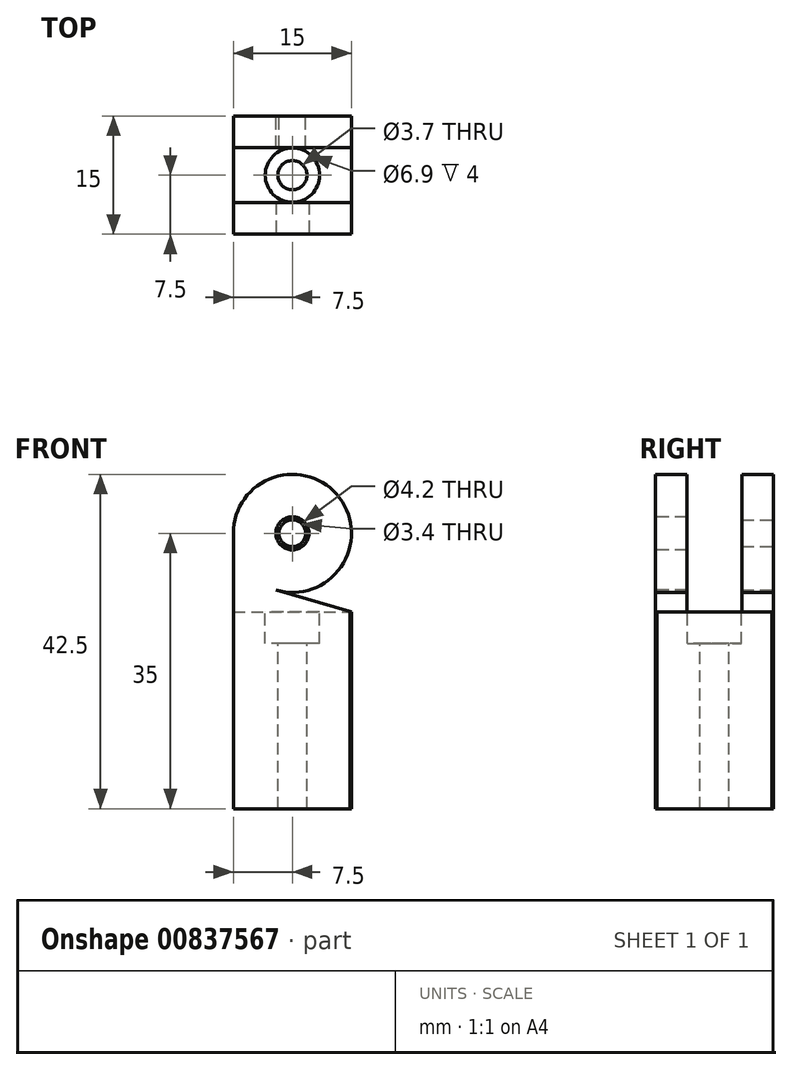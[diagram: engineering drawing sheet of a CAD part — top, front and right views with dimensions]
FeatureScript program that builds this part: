
annotation { "Feature Type Name" : "Feature", "Feature Type Description" : "" }
export const myFeature = defineFeature(function(context is Context, id is Id, definition is map)
    precondition{}
    {
        {
            var Q0;
            Q0=qCreatedBy(makeId("Top.planeOp"),FACE);
            var sketch = newSketch(context, id + "F0", { "sketchPlane" : qUnion([Q0])});
            skLineSegment(sketch, "E0", {"start": v(0, 0) * mm, "end": v(7.5, 0) * mm});
            skLineSegment(sketch, "E1", {"start": v(7.5, 0) * mm, "end": v(7.5, 7.5) * mm});
            skLineSegment(sketch, "E2", {"start": v(7.5, 7.5) * mm, "end": v(-7.5, 7.5) * mm});
            skLineSegment(sketch, "E3", {"start": v(-7.5, 7.5) * mm, "end": v(-7.5, -7.5) * mm});
            skLineSegment(sketch, "E4", {"start": v(-7.5, -7.5) * mm, "end": v(7.5, -7.5) * mm});
            skLineSegment(sketch, "E5", {"start": v(7.5, -7.5) * mm, "end": v(7.5, 0) * mm});
            skSolve(sketch);
        }
        {
            var Q0;
            Q0=makeQuery(id+"F0.imprint","IMPRINT",FACE,{"disambiguationData":[TD([[makeQuery(id+"F0.imprint","IMPRINT",EDGE,{"derivedFrom":sQuery(id+"F0.wireOp",EDGE,"E1")}),1.0]])]});
            extrude(context, id + "F1", {"entities" : qUnion([Q0]), "depth" : 25 * mm, "offsetDistance" : 25 * mm});
        }
        {
            var Q0;
            Q0=makeQuery(id+"F1.opExtrude","CAP_FACE",FACE,{"disambiguationData":[OSD([sQuery(id+"F0.wireOp",EDGE,"E1"),sQuery(id+"F0.wireOp",EDGE,"E2"),sQuery(id+"F0.wireOp",EDGE,"E3"),sQuery(id+"F0.wireOp",EDGE,"E4"),sQuery(id+"F0.wireOp",EDGE,"E5")])],"isStart":false});
            var sketch = newSketch(context, id + "F2", { "sketchPlane" : qUnion([Q0])});
            skPoint(sketch, "E6", {"position": v(0, 0) * mm});
            skSolve(sketch);
        }
        {
            var Q0;
            Q0=sQuery(id+"F2.wireOp",VERTEX,"E6");
            var Q1;
            Q1=makeQuery(id+"F1.opExtrude","SWEPT_BODY",BODY,{"disambiguationData":[OSD([sQuery(id+"F0.wireOp",EDGE,"E1"),sQuery(id+"F0.wireOp",EDGE,"E2"),sQuery(id+"F0.wireOp",EDGE,"E3"),sQuery(id+"F0.wireOp",EDGE,"E4"),sQuery(id+"F0.wireOp",EDGE,"E5")])]});
            hole(context, id + "F3", {"style" : HoleStyle.C_BORE, "endStyle" : HoleEndStyle.THROUGH, "holeDiameter" : 3.7 * mm, "cBoreDiameter" : 6.9 * mm, "cBoreDepth" : 4 * mm, "majorDiameter" : 5 * mm, "isTappedThrough" : true, "tappedDepth" : 12 * mm, "tapClearance" : 3, "locations" : qUnion([Q0]), "scope" : qUnion([Q1])});
        }
        {
            var Q0;
            Q0=makeQuery(id+"F1.opExtrude","SWEPT_FACE",FACE,{"disambiguationData":[OSD([sQuery(id+"F0.wireOp",EDGE,"E2")])]});
            var sketch = newSketch(context, id + "F4", { "sketchPlane" : qUnion([Q0])});
            skLineSegment(sketch, "E7", {"start": v(7.5, 25) * mm, "end": v(7.5, 35) * mm});
            skLineSegment(sketch, "E8", {"start": v(7.5, 35) * mm, "end": v(0, 35) * mm});
            skCircle(sketch, "E9", {"center": v(0, 35) * mm, "radius": 7.5 * mm});
            skLineSegment(sketch, "E10", {"start": v(-7.5, 25) * mm, "end": v(2.1, 27.8) * mm});
            skSolve(sketch);
        }
        {
            var Q0;
            {var subQ0=sQuery(id+"F4.wireOp",EDGE,"E7");Q0=makeQuery(id+"F4.imprint","IMPRINT",FACE,{"disambiguationData":[TD([[makeQuery(id+"F4.imprint","IMPRINT",EDGE,{"derivedFrom":subQ0}),1.0]])]});}
            var Q1;
            {var subQ0=sQuery(id+"F4.wireOp",EDGE,"E9");var subQ1=makeQuery(id+"F4.imprint","INTERSECT",VERTEX,{"derivedFrom":[sQuery(id+"F4.wireOp",EDGE,"E7"),subQ0]});Q1=makeQuery(id+"F4.imprint","IMPRINT",FACE,{"disambiguationData":[TD([[makeQuery(id+"F4.imprint","IMPRINT",EDGE,{"disambiguationData":[TD([[subQ1,-1.0]])],"derivedFrom":subQ0}),1.0]])]});}
            extrude(context, id + "F5", {"entities" : qUnion([Q0, Q1]), "operationType" : NewBodyOperationType.ADD, "oppositeDirection" : true, "depth" : 4 * mm, "offsetDistance" : 25 * mm});
        }
        {
            var Q0;
            Q0=makeQuery(id+"F1.opExtrude","SWEPT_FACE",FACE,{"disambiguationData":[OSD([sQuery(id+"F0.wireOp",EDGE,"E4")])]});
            var sketch = newSketch(context, id + "F6", { "sketchPlane" : qUnion([Q0])});
            skLineSegment(sketch, "E11", {"start": v(-7.5, 25) * mm, "end": v(-7.5, 35) * mm});
            skLineSegment(sketch, "E12", {"start": v(-7.5, 35) * mm, "end": v(0, 35) * mm});
            skCircle(sketch, "E13", {"center": v(0, 35) * mm, "radius": 7.5 * mm});
            skLineSegment(sketch, "E14", {"start": v(7.5, 25) * mm, "end": v(-2.1, 27.8) * mm});
            skSolve(sketch);
        }
        {
            var Q0;
            {var subQ0=sQuery(id+"F6.wireOp",EDGE,"E13");var subQ1=makeQuery(id+"F6.imprint","INTERSECT",VERTEX,{"derivedFrom":[sQuery(id+"F6.wireOp",EDGE,"E11"),subQ0]});Q0=makeQuery(id+"F6.imprint","IMPRINT",FACE,{"disambiguationData":[TD([[makeQuery(id+"F6.imprint","IMPRINT",EDGE,{"disambiguationData":[TD([[subQ1,-1.0]])],"derivedFrom":subQ0}),1.0]])]});}
            var Q1;
            {var subQ0=sQuery(id+"F6.wireOp",EDGE,"E11");Q1=makeQuery(id+"F6.imprint","IMPRINT",FACE,{"disambiguationData":[TD([[makeQuery(id+"F6.imprint","IMPRINT",EDGE,{"derivedFrom":subQ0}),-1.0]])]});}
            extrude(context, id + "F7", {"entities" : qUnion([Q0, Q1]), "operationType" : NewBodyOperationType.ADD, "oppositeDirection" : true, "depth" : 4 * mm, "offsetDistance" : 25 * mm});
        }
        {
            var Q0;
            {var subQ0=sQuery(id+"F0.wireOp",EDGE,"E4");Q0=makeQuery(id+"F7.boolean.opBoolean","MERGE",FACE,{"derivedFrom":[makeQuery(id+"F1.opExtrude","SWEPT_FACE",FACE,{"disambiguationData":[OSD([subQ0])]}),makeQuery(id+"F7.opExtrude","CAP_FACE",FACE,{"disambiguationData":[OSD([subQ0,sQuery(id+"F6.wireOp",EDGE,"E11"),sQuery(id+"F6.wireOp",EDGE,"E13"),sQuery(id+"F6.wireOp",EDGE,"E14")])],"isStart":true})]});}
            var sketch = newSketch(context, id + "F8", { "sketchPlane" : qUnion([Q0])});
            skLineSegment(sketch, "E15", {"start": v(-7.5, 35) * mm, "end": v(0, 35) * mm});
            skPoint(sketch, "E16", {"position": v(0, 35) * mm});
            skSolve(sketch);
        }
        {
            var Q0;
            Q0=sQuery(id+"F8.wireOp",VERTEX,"E16");
            var Q1;
            Q1=makeQuery(id+"F1.opExtrude","SWEPT_BODY",BODY,{"disambiguationData":[OSD([sQuery(id+"F0.wireOp",EDGE,"E1"),sQuery(id+"F0.wireOp",EDGE,"E2"),sQuery(id+"F0.wireOp",EDGE,"E3"),sQuery(id+"F0.wireOp",EDGE,"E4"),sQuery(id+"F0.wireOp",EDGE,"E5")])]});
            hole(context, id + "F9", {"style" : HoleStyle.SIMPLE, "endStyle" : HoleEndStyle.BLIND, "holeDiameter" : 4.2 * mm, "majorDiameter" : 5 * mm, "holeDepth" : 4 * mm, "isTappedThrough" : true, "tappedDepth" : 12 * mm, "tapClearance" : 3, "locations" : qUnion([Q0]), "scope" : qUnion([Q1])});
        }
        {
            var Q0;
            {var subQ0=sQuery(id+"F0.wireOp",EDGE,"E2");Q0=makeQuery(id+"F5.boolean.opBoolean","MERGE",FACE,{"derivedFrom":[makeQuery(id+"F1.opExtrude","SWEPT_FACE",FACE,{"disambiguationData":[OSD([subQ0])]}),makeQuery(id+"F5.opExtrude","CAP_FACE",FACE,{"disambiguationData":[OSD([subQ0,sQuery(id+"F4.wireOp",EDGE,"E7"),sQuery(id+"F4.wireOp",EDGE,"E9"),sQuery(id+"F4.wireOp",EDGE,"E10")])],"isStart":true})]});}
            var sketch = newSketch(context, id + "F10", { "sketchPlane" : qUnion([Q0])});
            skLineSegment(sketch, "E17", {"start": v(7.5, 35) * mm, "end": v(0, 35) * mm});
            skPoint(sketch, "E18", {"position": v(0, 35) * mm});
            skSolve(sketch);
        }
        {
            var Q0;
            Q0=sQuery(id+"F10.wireOp",VERTEX,"E18");
            var Q1;
            Q1=makeQuery(id+"F1.opExtrude","SWEPT_BODY",BODY,{"disambiguationData":[OSD([sQuery(id+"F0.wireOp",EDGE,"E1"),sQuery(id+"F0.wireOp",EDGE,"E2"),sQuery(id+"F0.wireOp",EDGE,"E3"),sQuery(id+"F0.wireOp",EDGE,"E4"),sQuery(id+"F0.wireOp",EDGE,"E5")])]});
            hole(context, id + "F11", {"style" : HoleStyle.SIMPLE, "endStyle" : HoleEndStyle.BLIND, "holeDiameter" : 3.4 * mm, "majorDiameter" : 5 * mm, "holeDepth" : 4 * mm, "isTappedThrough" : true, "tappedDepth" : 12 * mm, "tapClearance" : 3, "locations" : qUnion([Q0]), "scope" : qUnion([Q1])});
        }
        {
            var Q0;
            Q0=makeQuery(id+"F1.opExtrude","SWEPT_EDGE",EDGE,{"disambiguationData":[OSD([sQuery(id+"F0.wireOp",EDGE,"E4"),sQuery(id+"F0.wireOp",EDGE,"E5")])]});
            var Q1;
            Q1=makeQuery(id+"F1.opExtrude","SWEPT_EDGE",EDGE,{"disambiguationData":[OSD([sQuery(id+"F0.wireOp",EDGE,"E1"),sQuery(id+"F0.wireOp",EDGE,"E2")])]});
            chamfer(context, id + "F12", {"entities" : qUnion([Q0, Q1]), "width" : .2 * mm, "tangentPropagation" : true});
        }
    });
